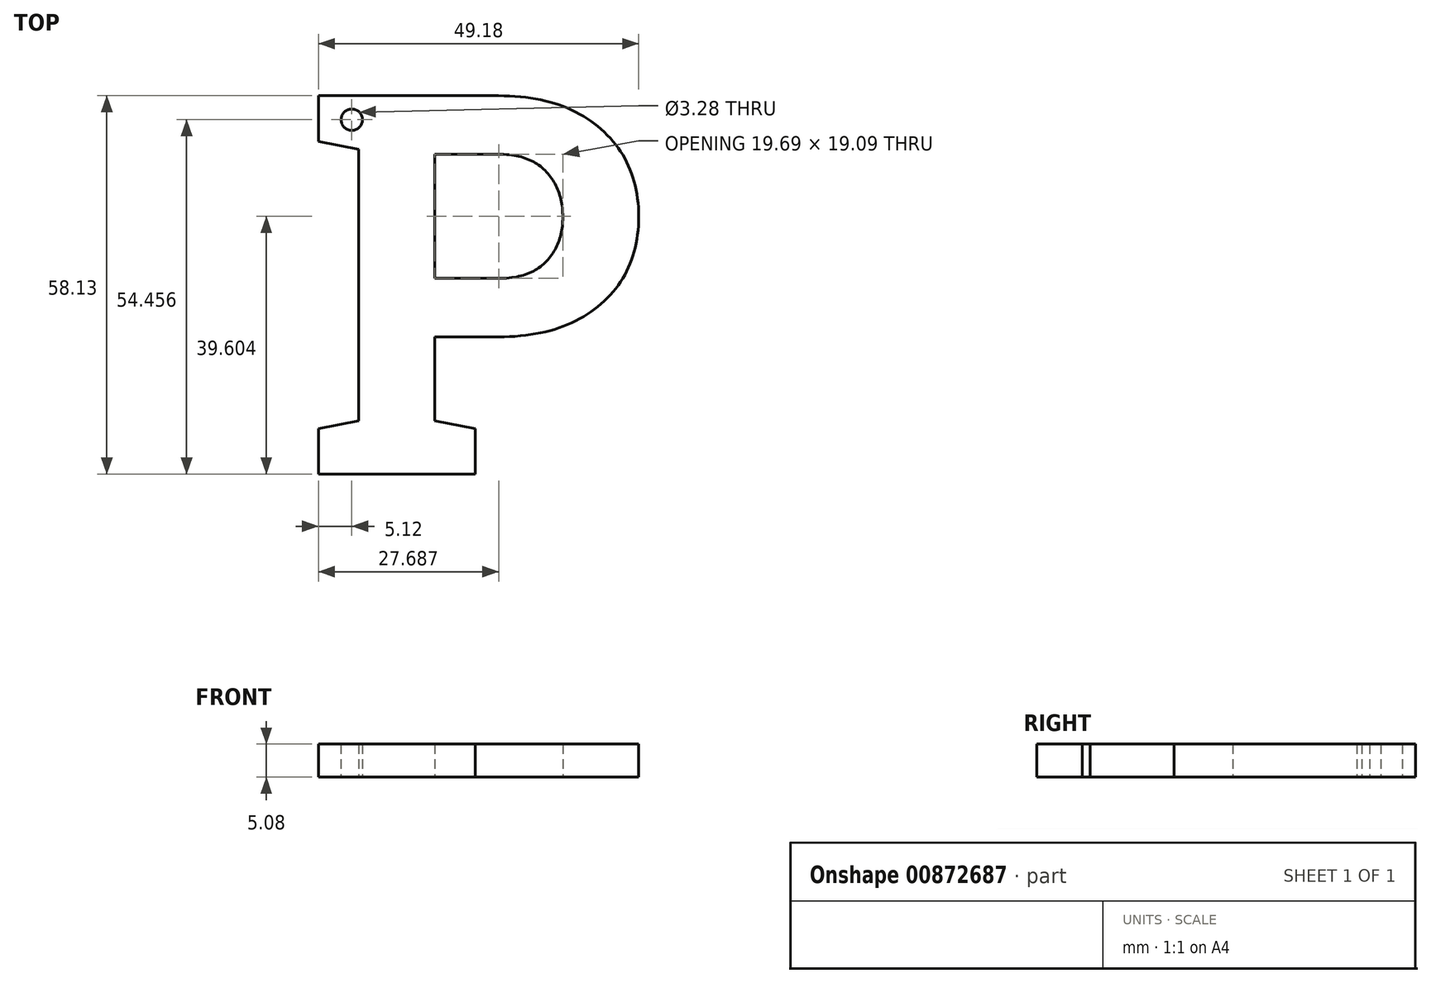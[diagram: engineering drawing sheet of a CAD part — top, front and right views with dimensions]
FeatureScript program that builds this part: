
annotation { "Feature Type Name" : "Feature", "Feature Type Description" : "" }
export const myFeature = defineFeature(function(context is Context, id is Id, definition is map)
    precondition{}
    {
        {
            var Q0;
            Q0=qCreatedBy(makeId("Top.planeOp"),FACE);
            var sketch = newSketch(context, id + "F0", { "sketchPlane" : qUnion([Q0])});
            skText(sketch, "E0", { "text": "P", "fontName": "RobotoSlab-Bold.ttf"});
            skCircle(sketch, "E1", {"center": v(-12.5, 22.5) * mm, "radius": 1.64 * mm});
            const initialGuessF0  = {"E0": [-0.01987, -0.03196, 1, 0, 0.05887]};
            skSetInitialGuess(sketch, initialGuessF0);
            skSolve(sketch);
        }
        {
            var Q0;
            Q0 = qSketchRegion(id + "F0", true);
            extrude(context, id + "F1", {"entities" : qUnion([Q0]), "depth" : 5.08 * mm, "offsetDistance" : 25.4 * mm});
        }
    });
